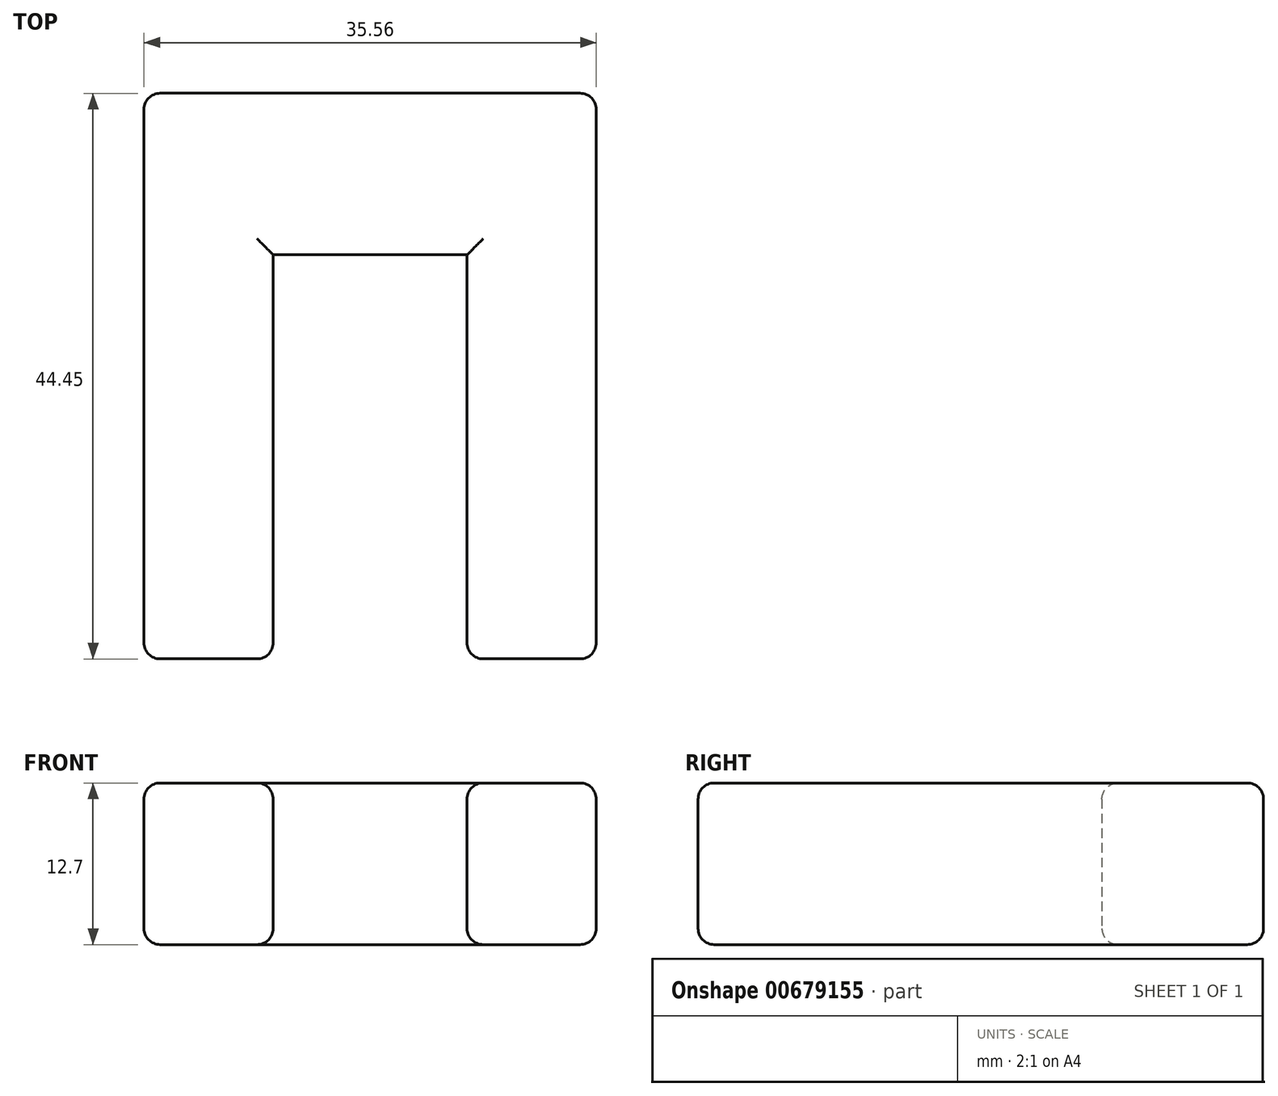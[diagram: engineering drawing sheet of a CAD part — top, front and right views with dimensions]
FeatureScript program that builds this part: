
annotation { "Feature Type Name" : "Feature", "Feature Type Description" : "" }
export const myFeature = defineFeature(function(context is Context, id is Id, definition is map)
    precondition{}
    {
        {
            var Q0;
            Q0=qCreatedBy(makeId("Top.planeOp"),FACE);
            var sketch = newSketch(context, id + "F0", { "sketchPlane" : qUnion([Q0])});
            skLineSegment(sketch, "E0", {"start": v(0, 15.51) * mm, "end": v(-17.78, 15.51) * mm});
            skLineSegment(sketch, "E1", {"start": v(-17.78, 15.51) * mm, "end": v(-17.78, -28.94) * mm});
            skLineSegment(sketch, "E2", {"start": v(-17.78, -28.94) * mm, "end": v(-7.62, -28.94) * mm});
            skLineSegment(sketch, "E3", {"start": v(-7.62, -28.94) * mm, "end": v(-7.62, 2.81) * mm});
            skLineSegment(sketch, "E4", {"start": v(-7.62, 2.81) * mm, "end": v(0, 2.81) * mm});
            skLineSegment(sketch, "E5", {"start": v(0, 2.81) * mm, "end": v(0, 15.51) * mm});
            skLineSegment(sketch, "E6.MirrorCS", {"start": v(0, 15.51) * mm, "end": v(17.78, 15.51) * mm});
            skLineSegment(sketch, "E7.MirrorCS", {"start": v(17.78, 15.51) * mm, "end": v(17.78, -28.94) * mm});
            skLineSegment(sketch, "E8.MirrorCS", {"start": v(17.78, -28.94) * mm, "end": v(7.62, -28.94) * mm});
            skLineSegment(sketch, "E9.MirrorCS", {"start": v(7.62, -28.94) * mm, "end": v(7.62, 2.81) * mm});
            skLineSegment(sketch, "E10.MirrorCS", {"start": v(7.62, 2.81) * mm, "end": v(0, 2.81) * mm});
            skSolve(sketch);
        }
        {
            var Q0;
            Q0 = qSketchRegion(id + "F0", true);
            extrude(context, id + "F1", {"entities" : qUnion([Q0]), "depth" : 12.7 * mm, "offsetDistance" : 25.4 * mm});
        }
        {
            var Q0;
            Q0=makeQuery(id+"F1.opExtrude","CAP_EDGE",EDGE,{"disambiguationData":[OSD([sQuery(id+"F0.wireOp",EDGE,"E1")])],"isStart":false});
            var Q1;
            Q1=makeQuery(id+"F1.opExtrude","CAP_FACE",FACE,{"disambiguationData":[OSD([sQuery(id+"F0.wireOp",EDGE,"E0"),sQuery(id+"F0.wireOp",EDGE,"E1"),sQuery(id+"F0.wireOp",EDGE,"E2"),sQuery(id+"F0.wireOp",EDGE,"E3"),sQuery(id+"F0.wireOp",EDGE,"E4"),sQuery(id+"F0.wireOp",EDGE,"E6.MirrorCS"),sQuery(id+"F0.wireOp",EDGE,"E7.MirrorCS"),sQuery(id+"F0.wireOp",EDGE,"E8.MirrorCS"),sQuery(id+"F0.wireOp",EDGE,"E9.MirrorCS"),sQuery(id+"F0.wireOp",EDGE,"E10.MirrorCS")])],"isStart":false});
            var Q2;
            Q2=makeQuery(id+"F1.opExtrude","CAP_FACE",FACE,{"disambiguationData":[OSD([sQuery(id+"F0.wireOp",EDGE,"E0"),sQuery(id+"F0.wireOp",EDGE,"E1"),sQuery(id+"F0.wireOp",EDGE,"E2"),sQuery(id+"F0.wireOp",EDGE,"E3"),sQuery(id+"F0.wireOp",EDGE,"E4"),sQuery(id+"F0.wireOp",EDGE,"E6.MirrorCS"),sQuery(id+"F0.wireOp",EDGE,"E7.MirrorCS"),sQuery(id+"F0.wireOp",EDGE,"E8.MirrorCS"),sQuery(id+"F0.wireOp",EDGE,"E9.MirrorCS"),sQuery(id+"F0.wireOp",EDGE,"E10.MirrorCS")])],"isStart":true});
            var Q3;
            Q3=makeQuery(id+"F1.opExtrude","SWEPT_EDGE",EDGE,{"disambiguationData":[OSD([sQuery(id+"F0.wireOp",EDGE,"E7.MirrorCS"),sQuery(id+"F0.wireOp",EDGE,"E8.MirrorCS")])]});
            var Q4;
            Q4=makeQuery(id+"F1.opExtrude","SWEPT_EDGE",EDGE,{"disambiguationData":[OSD([sQuery(id+"F0.wireOp",EDGE,"E8.MirrorCS"),sQuery(id+"F0.wireOp",EDGE,"E9.MirrorCS")])]});
            var Q5;
            Q5=makeQuery(id+"F1.opExtrude","SWEPT_EDGE",EDGE,{"disambiguationData":[OSD([sQuery(id+"F0.wireOp",EDGE,"E2"),sQuery(id+"F0.wireOp",EDGE,"E3")])]});
            var Q6;
            Q6=makeQuery(id+"F1.opExtrude","SWEPT_EDGE",EDGE,{"disambiguationData":[OSD([sQuery(id+"F0.wireOp",EDGE,"E1"),sQuery(id+"F0.wireOp",EDGE,"E2")])]});
            var Q7;
            Q7=makeQuery(id+"F1.opExtrude","SWEPT_EDGE",EDGE,{"disambiguationData":[OSD([sQuery(id+"F0.wireOp",EDGE,"E0"),sQuery(id+"F0.wireOp",EDGE,"E1")])]});
            var Q8;
            Q8=makeQuery(id+"F1.opExtrude","SWEPT_EDGE",EDGE,{"disambiguationData":[OSD([sQuery(id+"F0.wireOp",EDGE,"E6.MirrorCS"),sQuery(id+"F0.wireOp",EDGE,"E7.MirrorCS")])]});
            fillet(context, id + "F2", {"entities" : qUnion([Q0, Q1, Q2, Q3, Q4, Q5, Q6, Q7, Q8]), "radius" : 1.27 * mm, "tangentPropagation" : true, "allowEdgeOverflow" : false});
        }
    });
